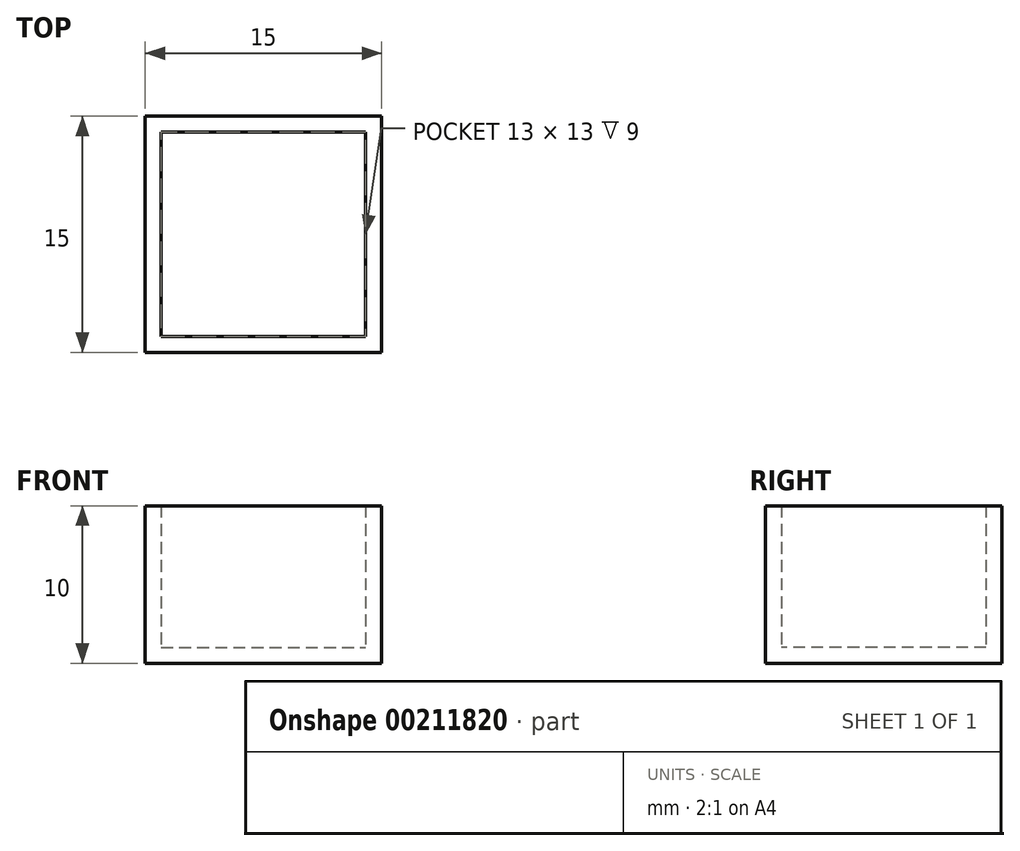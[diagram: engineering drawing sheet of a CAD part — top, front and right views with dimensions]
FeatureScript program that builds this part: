
annotation { "Feature Type Name" : "Feature", "Feature Type Description" : "" }
export const myFeature = defineFeature(function(context is Context, id is Id, definition is map)
    precondition{}
    {
        {
            var Q0;
            Q0=qCreatedBy(makeId("Top.planeOp"),FACE);
            var sketch = newSketch(context, id + "F0", { "sketchPlane" : qUnion([Q0])});
            skLineSegment(sketch, "E0.bottom", {"start": v(-7.5, 7.5) * mm, "end": v(7.5, 7.5) * mm});
            skLineSegment(sketch, "E0.top", {"start": v(-7.5, -7.5) * mm, "end": v(7.5, -7.5) * mm});
            skLineSegment(sketch, "E0.left", {"start": v(-7.5, 7.5) * mm, "end": v(-7.5, -7.5) * mm});
            skLineSegment(sketch, "E0.right", {"start": v(7.5, 7.5) * mm, "end": v(7.5, -7.5) * mm});
            skPoint(sketch, "E0.middle", {"position": v(0, 0) * mm});
            skSolve(sketch);
        }
        {
            var Q0;
            Q0 = qSketchRegion(id + "F0", true);
            extrude(context, id + "F1", {"entities" : qUnion([Q0]), "flatOperationType" : FlatOperationType.REMOVE, "offsetDistance" : 25 * mm, "depth" : 10 * mm, "domain" : OperationDomain.MODEL});
        }
        {
            var Q0;
            Q0=makeQuery(id+"F1.opExtrude","CAP_FACE",FACE,{"disambiguationData":[OSD([sQuery(id+"F0.wireOp",EDGE,"E0.bottom"),sQuery(id+"F0.wireOp",EDGE,"E0.top"),sQuery(id+"F0.wireOp",EDGE,"E0.left"),sQuery(id+"F0.wireOp",EDGE,"E0.right")])],"isStart":false});
            shell(context, id + "F2", {"entities" : qUnion([Q0]), "thickness" : 1 * mm});
        }
    });
